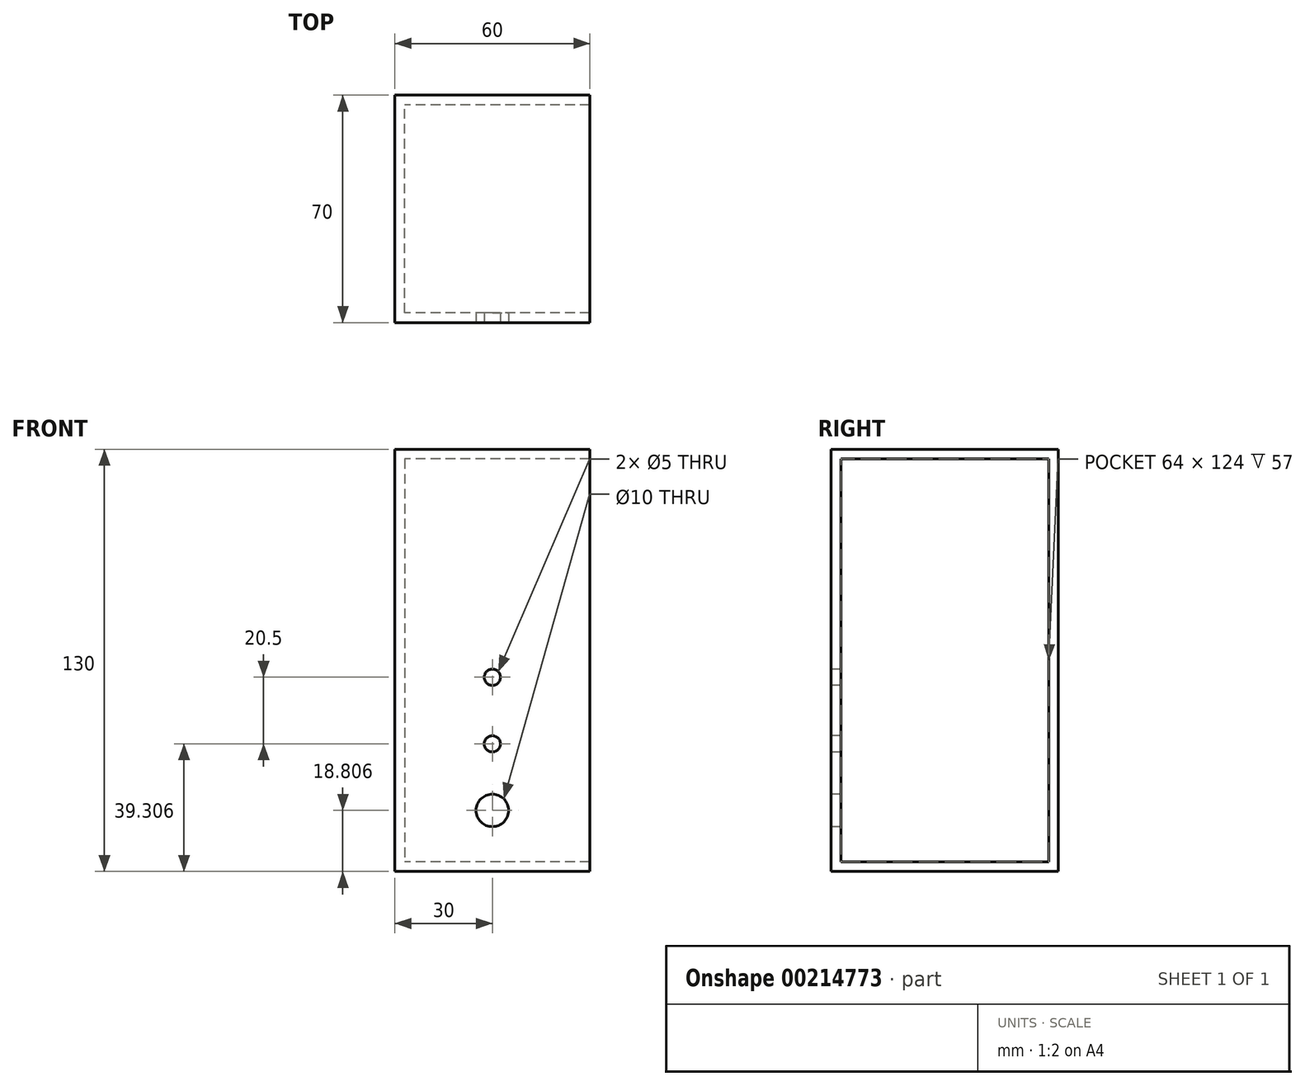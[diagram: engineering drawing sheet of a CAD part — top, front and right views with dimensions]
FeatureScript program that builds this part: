
annotation { "Feature Type Name" : "Feature", "Feature Type Description" : "" }
export const myFeature = defineFeature(function(context is Context, id is Id, definition is map)
    precondition{}
    {
        {
            var Q0;
            Q0=qCreatedBy(makeId("Right.planeOp"),FACE);
            var sketch = newSketch(context, id + "F0", { "sketchPlane" : qUnion([Q0])});
            skLineSegment(sketch, "E0.bottom", {"start": v(-4.98, 121.22) * mm, "end": v(65.02, 121.22) * mm});
            skLineSegment(sketch, "E0.top", {"start": v(-4.98, -8.78) * mm, "end": v(65.02, -8.78) * mm});
            skLineSegment(sketch, "E0.left", {"start": v(-4.98, 121.22) * mm, "end": v(-4.98, -8.78) * mm});
            skLineSegment(sketch, "E0.right", {"start": v(65.02, 121.22) * mm, "end": v(65.02, -8.78) * mm});
            skSolve(sketch);
        }
        {
            var Q0;
            Q0 = qSketchRegion(id + "F0", true);
            extrude(context, id + "F1", {"entities" : qUnion([Q0]), "depth" : 60 * mm});
        }
        {
            var Q0;
            Q0=makeQuery(id+"F1.opExtrude","CAP_FACE",FACE,{"disambiguationData":[OSD([sQuery(id+"F0.wireOp",EDGE,"E0.bottom"),sQuery(id+"F0.wireOp",EDGE,"E0.top"),sQuery(id+"F0.wireOp",EDGE,"E0.left"),sQuery(id+"F0.wireOp",EDGE,"E0.right")])],"isStart":false});
            shell(context, id + "F2", {"entities" : qUnion([Q0]), "thickness" : 3 * mm});
        }
        {
            var Q0;
            Q0=makeQuery(id+"F1.opExtrude","SWEPT_FACE",FACE,{"disambiguationData":[OSD([sQuery(id+"F0.wireOp",EDGE,"E0.left")])]});
            var sketch = newSketch(context, id + "F3", { "sketchPlane" : qUnion([Q0])});
            skCircle(sketch, "E1", {"center": v(30, 10.03) * mm, "radius": 5 * mm});
            skCircle(sketch, "E2", {"center": v(30, 30.53) * mm, "radius": 2.5 * mm});
            skCircle(sketch, "E3", {"center": v(30, 51.03) * mm, "radius": 2.5 * mm});
            skSolve(sketch);
        }
        {
            var Q0;
            Q0 = qSketchRegion(id + "F3", true);
            extrude(context, id + "F4", {"entities" : qUnion([Q0]), "operationType" : NewBodyOperationType.REMOVE, "endBound" : BoundingType.UP_TO_NEXT, "oppositeDirection" : true, "depth" : 25 * mm});
        }
    });
